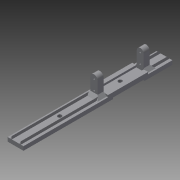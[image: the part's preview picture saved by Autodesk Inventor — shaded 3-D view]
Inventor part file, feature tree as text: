
AUTODESK INVENTOR PART (.ipt)
format: ipt  version: 2015 (Build 190159000, 159)  size: 215,552 bytes
history: native  units: in
note: dims shown in document units (in); Inventor stores cm internally (conversion verified against a paired STEP export)
features: reference x9, extrude x8, sketch x8, projected_geometry x3, chamfer x2, fillet x1
ambient origin geometry x8: Origin, YZ Plane, XZ Plane, XY Plane, X Axis, Y Axis, Z Axis, Center Point
bodies: Solid1 (feature_tree)
feature tree (31):
  extrude  "Extrusion1"  Depth=0.25in
  extrude  "Extrusion2"  Depth=0.25in
  extrude  "Extrusion3"  Depth=0.25in TaperAngle=0.0deg
  extrude  "Extrusion4"  Depth=2.075in TaperAngle=0.0deg
  chamfer  "Chamfer1"  Distance=1.1875in
  extrude  "Extrusion5"  Depth=0.125in TaperAngle=0.0deg
  fillet  "Fillet1"  Radius=0.25in
  chamfer  "Chamfer2"  Distance=0.125in Angle=45.0deg
  extrude  "Extrusion6"  Depth=0.125in TaperAngle=0.0deg
  extrude  "Extrusion7"  Depth=0.125in TaperAngle=0.0deg
  extrude  "Extrusion8"  [1 undecoded]
  sketch  "Sketch1"  dims[d0=1.0in d1=0.25in]
  sketch  "Sketch2"  dims[d2=9.3625in d3=0.0in d6=0.25in]
  projected_geometry  "Projected Loop1"
  sketch  "Sketch3"  dims[d7=0.25in d8=4.8in d9=0.0in]
  sketch  "Sketch4"  dims[d10=3.8in d11=2.075in d12=0.0in]
  reference  "Reference1"
  reference  "Reference2"
  sketch  "Sketch5"  dims[d13=0.375in]
  reference  "Reference3"
  reference  "Reference4"
  sketch  "Sketch6"  dims[d14=0.375in d15=1.1875in d16=0.0in]
  sketch  "Sketch7"  dims[d17=0.1875in d18=0.125in d19=45.0deg d20=1.25in d21=0.0in d22=0.25in d23=0.1875in d24=0.125in d25=45.0deg]
  reference  "Reference5"
  reference  "Reference6"
  reference  "Reference7"
  sketch  "Sketch8"  dims[d26=0.1875in d27=-0.1374in d28=0.125in d29=0.0in d30=0.125in d31=0.0in]
  projected_geometry  "Projected Loop2"
  projected_geometry  "Projected Loop3"
  reference  "Reference8"
  reference  "Reference9"
note: 1 required parameter value undecoded (feature->parameter linkage not recoverable at this tier; creation-order binding heuristic only, values carry confidence <= 0.55)
